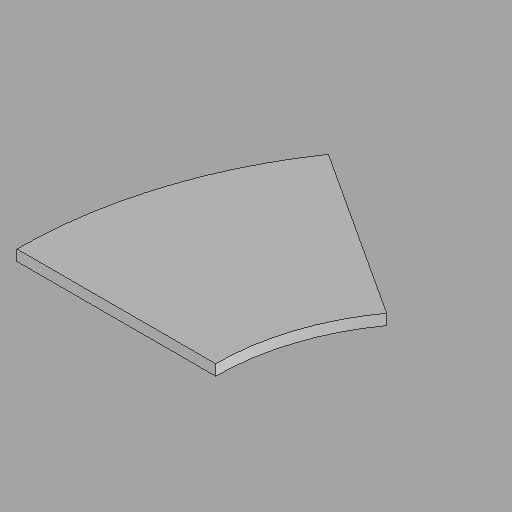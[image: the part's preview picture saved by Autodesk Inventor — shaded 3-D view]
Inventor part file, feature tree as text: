
AUTODESK INVENTOR PART (.ipt)
format: ipt  version: 2022.2 (Build 262287010, 287A)  size: 110,592 bytes
history: native  units: in
note: dims shown in document units (in); Inventor stores cm internally (conversion verified against a paired STEP export)
features: direct_edit x1, revolve x1
ambient origin geometry x8: Origin, YZ Plane, XZ Plane, XY Plane, X Axis, Y Axis, Z Axis, Center Point
bodies: Solid1 (feature_tree)
feature tree (2):
  direct_edit  "Direct Edit1"
  revolve  "Rotate1"  [1 undecoded]
note: 1 required parameter value undecoded (feature->parameter linkage not recoverable at this tier; creation-order binding heuristic only, values carry confidence <= 0.55)
